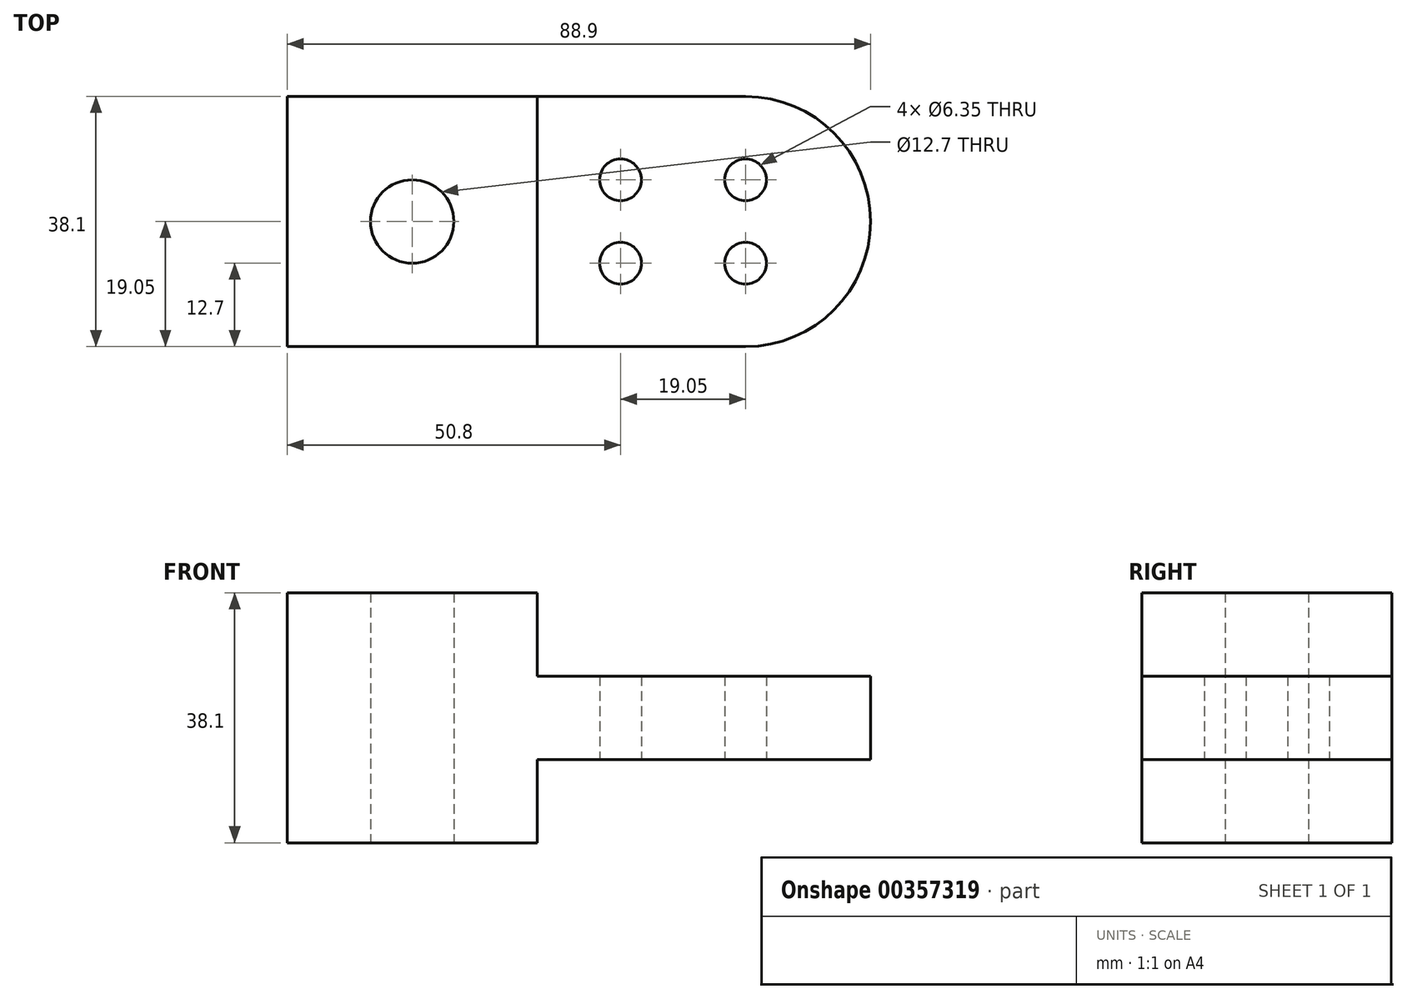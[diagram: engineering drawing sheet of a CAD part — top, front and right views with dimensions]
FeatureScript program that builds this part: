
annotation { "Feature Type Name" : "Feature", "Feature Type Description" : "" }
export const myFeature = defineFeature(function(context is Context, id is Id, definition is map)
    precondition{}
    {
        {
            var Q0;
            Q0=qCreatedBy(makeId("Top.planeOp"),FACE);
            var sketch = newSketch(context, id + "F0", { "sketchPlane" : qUnion([Q0])});
            skLineSegment(sketch, "E0.bottom", {"start": v(-19.05, 19.05) * mm, "end": v(19.05, 19.05) * mm});
            skLineSegment(sketch, "E0.top", {"start": v(-19.05, -19.05) * mm, "end": v(19.05, -19.05) * mm});
            skLineSegment(sketch, "E0.left", {"start": v(-19.05, 19.05) * mm, "end": v(-19.05, -19.05) * mm});
            skLineSegment(sketch, "E0.right", {"start": v(19.05, 19.05) * mm, "end": v(19.05, -19.05) * mm});
            skCircle(sketch, "E1", {"center": v(0, 0) * mm, "radius": 6.35 * mm});
            skSolve(sketch);
        }
        {
            var Q0;
            Q0=makeQuery(id+"F0.imprint","IMPRINT",FACE,{"disambiguationData":[TD([[makeQuery(id+"F0.imprint","IMPRINT",EDGE,{"derivedFrom":sQuery(id+"F0.wireOp",EDGE,"E0.bottom")}),-1.0]])]});
            extrude(context, id + "F1", {"entities" : qUnion([Q0]), "endBound" : BoundingType.SYMMETRIC, "depth" : 38.1 * mm});
        }
        {
            var Q0;
            Q0=qCreatedBy(makeId("Top.planeOp"),FACE);
            var sketch = newSketch(context, id + "F2", { "sketchPlane" : qUnion([Q0])});
            skLineSegment(sketch, "E2", {"start": v(19.05, 19.05) * mm, "end": v(19.05, -19.05) * mm});
            skLineSegment(sketch, "E3", {"start": v(19.05, 19.05) * mm, "end": v(50.8, 19.05) * mm});
            skLineSegment(sketch, "E4", {"start": v(19.05, -19.05) * mm, "end": v(50.8, -19.05) * mm});
            skArc(sketch, "E5", {"start": v(50.8, -19.05) * mm, "mid": v(69.85, 0) * mm, "end": v(50.8, 19.05) * mm});
            skCircle(sketch, "E6", {"center": v(31.75, 6.35) * mm, "radius": 3.18 * mm});
            skCircle(sketch, "E7", {"center": v(50.8, 6.35) * mm, "radius": 3.18 * mm});
            skCircle(sketch, "E8", {"center": v(31.75, -6.35) * mm, "radius": 3.18 * mm});
            skCircle(sketch, "E9", {"center": v(50.8, -6.35) * mm, "radius": 3.18 * mm});
            skSolve(sketch);
        }
        {
            var Q0;
            Q0=qSketchRegion(id+"F2",true);
            extrude(context, id + "F3", {"entities" : qUnion([Q0]), "operationType" : NewBodyOperationType.ADD, "endBound" : BoundingType.SYMMETRIC, "depth" : 12.7 * mm});
        }
    });
